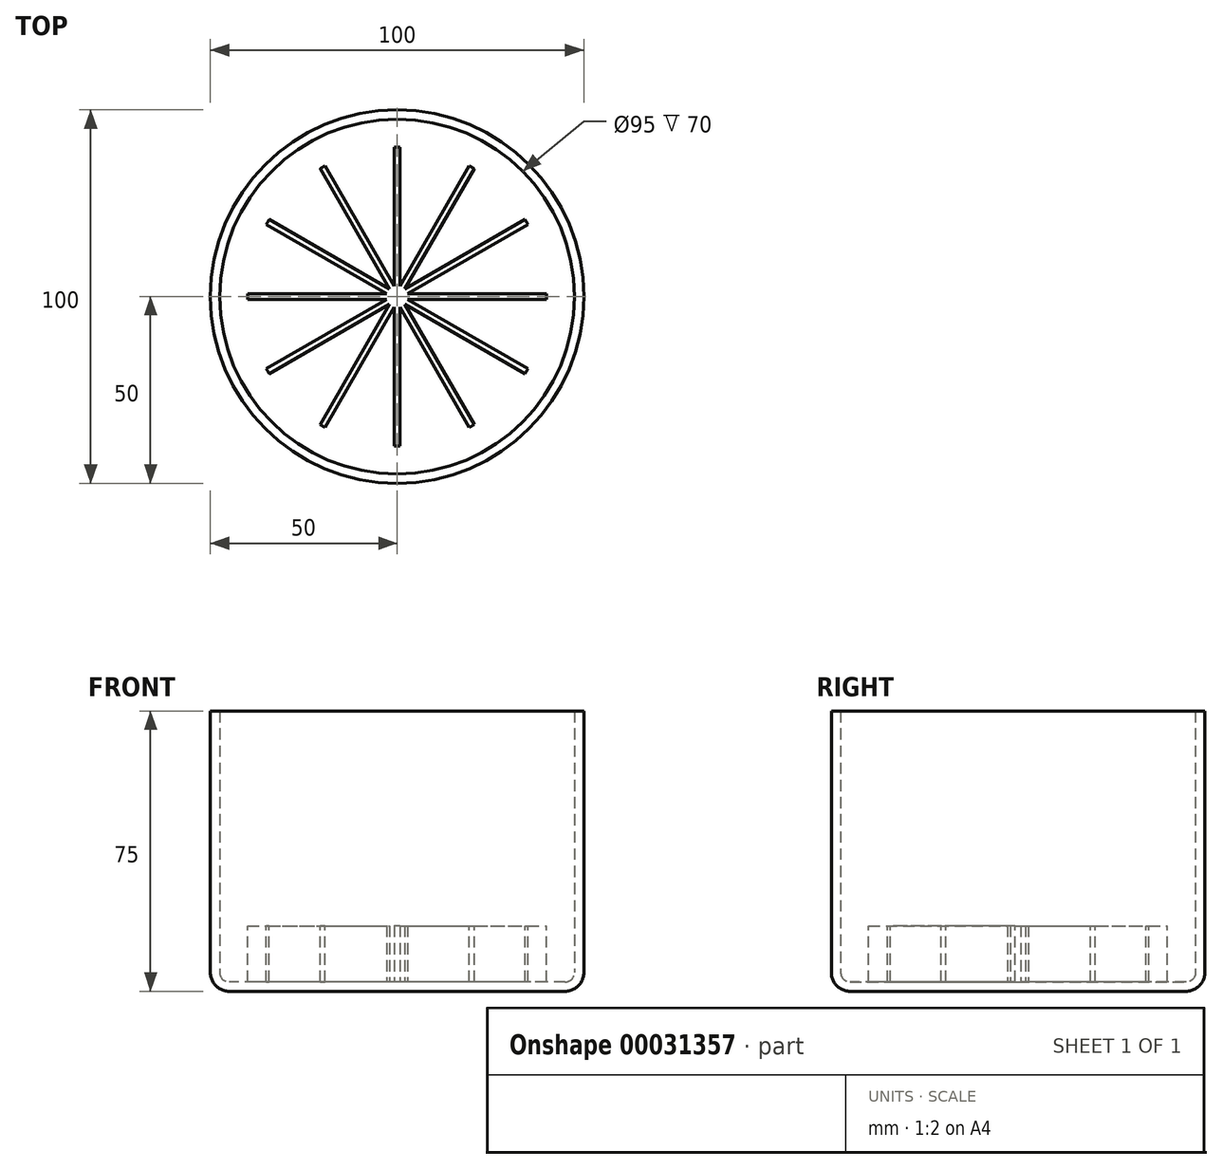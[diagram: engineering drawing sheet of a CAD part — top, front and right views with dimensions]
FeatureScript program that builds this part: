
annotation { "Feature Type Name" : "Feature", "Feature Type Description" : "" }
export const myFeature = defineFeature(function(context is Context, id is Id, definition is map)
    precondition{}
    {
        {
            var Q0;
            Q0=qCreatedBy(makeId("Top.planeOp"),FACE);
            var sketch = newSketch(context, id + "F0", { "sketchPlane" : qUnion([Q0])});
            skCircle(sketch, "E0", {"center": v(0, 0) * mm, "radius": 50 * mm});
            skSolve(sketch);
        }
        {
            var Q0;
            Q0=makeQuery(id+"F0.imprint","IMPRINT",FACE,{"disambiguationData":[TD([[makeQuery(id+"F0.imprint","IMPRINT",EDGE,{"derivedFrom":sQuery(id+"F0.wireOp",EDGE,"E0")}),1.0]])]});
            extrude(context, id + "F1", {"entities" : qUnion([Q0]), "endBound" : BoundingType.SYMMETRIC, "depth" : 75 * mm});
        }
        {
            var Q0;
            Q0=makeQuery(id+"F1.opExtrude","CAP_EDGE",EDGE,{"disambiguationData":[OSD([sQuery(id+"F0.wireOp",EDGE,"E0")])],"isStart":true});
            fillet(context, id + "F2", {"entities" : qUnion([Q0]), "radius" : 5 * mm, "tangentPropagation" : true, "allowEdgeOverflow" : false});
        }
        {
            var Q0;
            Q0=makeQuery(id+"F1.opExtrude","CAP_FACE",FACE,{"disambiguationData":[OSD([sQuery(id+"F0.wireOp",EDGE,"E0")])],"isStart":false});
            shell(context, id + "F3", {"entities" : qUnion([Q0]), "thickness" : 2.5 * mm});
        }
        {
            var Q0;
            Q0=qCreatedBy(makeId("Top.planeOp"),FACE);
            cPlane(context, id + "F4", {"entities" : qUnion([Q0]), "cplaneType" : CPlaneType.OFFSET, "offset" : 20 * mm, "oppositeDirection" : true, "width" : 150 * mm, "height" : 150 * mm});
        }
        {
            var Q0;
            Q0=qCreatedBy(id+"F4.planeOp",FACE);
            var sketch = newSketch(context, id + "F5", { "sketchPlane" : qUnion([Q0])});
            skLineSegment(sketch, "E1.rect.left", {"start": v(-0.75, -42.5) * mm, "end": v(-0.75, 42.5) * mm});
            skLineSegment(sketch, "E1.rect.right", {"start": v(0.75, -42.5) * mm, "end": v(0.75, 42.5) * mm});
            skPoint(sketch, "E1.rect.middle", {"position": v(0, 0) * mm});
            skArc(sketch, "E2.0", {"start": v(0.45, 42.5) * mm, "mid": v(-0.3, 42.5) * mm, "end": v(-1.05, 42.49) * mm});
            skArc(sketch, "E3.0", {"start": v(-0.75, -42.5) * mm, "mid": v(0, -42.5) * mm, "end": v(0.75, -42.5) * mm});
            skCircle(sketch, "E4.0", {"center": v(0, 0) * mm, "radius": 40 * mm});
            skPoint(sketch, "E1.rect.bottom.end.orphan", {"position": v(0.75, -49.2) * mm});
            skPoint(sketch, "E1.rect.bottom.start.orphan", {"position": v(-0.75, -49.2) * mm});
            skArc(sketch, "E5.trimOffspring", {"start": v(0.75, 42.5) * mm, "mid": v(0, 42.5) * mm, "end": v(-0.75, 42.5) * mm});
            skPoint(sketch, "E1.rect.top.end.orphan", {"position": v(0.75, 49.2) * mm});
            skPoint(sketch, "E1.rect.top.start.orphan", {"position": v(-0.75, 49.2) * mm});
            skSolve(sketch);
        }
        {
            var Q0;
            {var subQ0=sQuery(id+"F5.wireOp",EDGE,"E3.0");Q0=makeQuery(id+"F5.imprint","IMPRINT",FACE,{"disambiguationData":[TD([[makeQuery(id+"F5.imprint","IMPRINT",EDGE,{"derivedFrom":subQ0}),1.0]])]});}
            var Q1;
            {var subQ0=sQuery(id+"F5.wireOp",EDGE,"E4.0");var subQ3=sQuery(id+"F5.wireOp",EDGE,"E1.rect.left");var subQ6=makeQuery(id+"F5.imprint","INTERSECT",VERTEX,{"disambiguationData":[OD(0.0)],"derivedFrom":[subQ3,subQ0]});Q1=makeQuery(id+"F5.imprint","IMPRINT",FACE,{"disambiguationData":[TD([[makeQuery(id+"F5.imprint","IMPRINT",EDGE,{"disambiguationData":[TD([[subQ6,-1.0]])],"derivedFrom":subQ3}),-1.0]])]});}
            extrude(context, id + "F6", {"entities" : qUnion([Q0, Q1]), "endBound" : BoundingType.UP_TO_NEXT, "oppositeDirection" : true, "depth" : 25 * mm});
        }
        {
            var Q0;
            Q0=qCreatedBy(makeId("Right.planeOp"),FACE);
            var sketch = newSketch(context, id + "F7", { "sketchPlane" : qUnion([Q0])});
            skLineSegment(sketch, "E6", {"start": v(0, 56.07) * mm, "end": v(0, -58.6) * mm});
            skSolve(sketch);
        }
        {
            var Q0;
            Q0=makeQuery(id+"F6.opExtrude","SWEPT_BODY",BODY,{"disambiguationData":[OSD([sQuery(id+"F5.wireOp",EDGE,"E1.rect.left"),sQuery(id+"F5.wireOp",EDGE,"E1.rect.right"),sQuery(id+"F5.wireOp",EDGE,"E4.0"),sQuery(id+"F5.wireOp",EDGE,"E3.0")])]});
            var Q1;
            Q1=sQuery(id+"F7.wireOp",EDGE,"E6");
            circularPattern(context, id + "F8", {"operationType" : NewBodyOperationType.ADD, "entities" : qUnion([Q0]), "axis" : qUnion([Q1]), "angle" : 30 * degree, "instanceCount" : 6});
        }
    });
